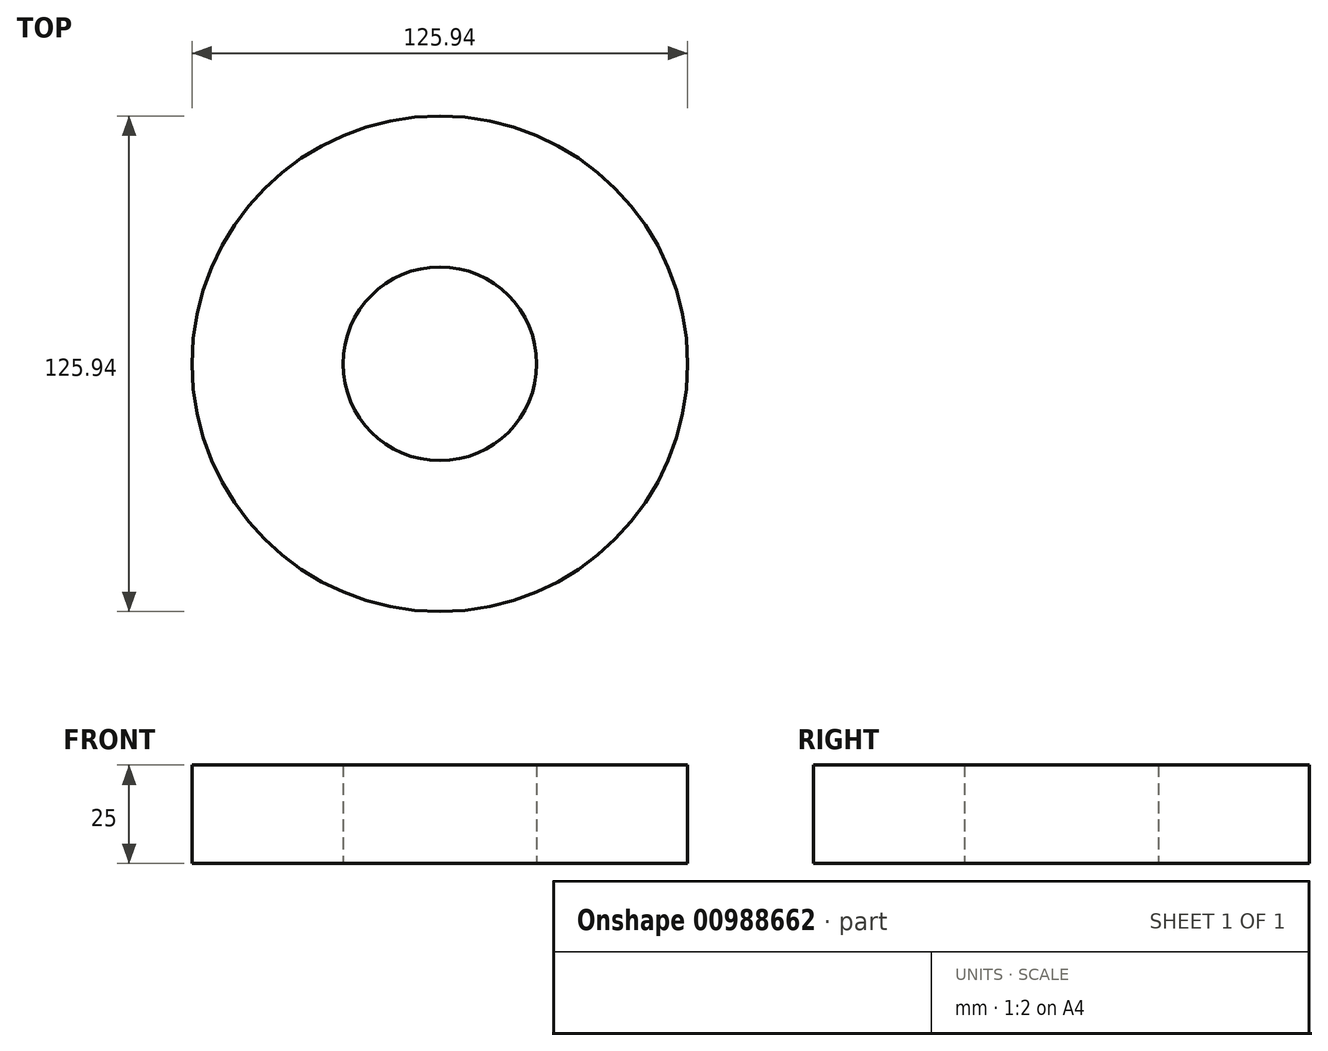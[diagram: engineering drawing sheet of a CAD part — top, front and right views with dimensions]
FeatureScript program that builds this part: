
annotation { "Feature Type Name" : "Feature", "Feature Type Description" : "" }
export const myFeature = defineFeature(function(context is Context, id is Id, definition is map)
    precondition{}
    {
        {
            var Q0;
            Q0=qCreatedBy(makeId("Top.planeOp"),FACE);
            var sketch = newSketch(context, id + "F0", { "sketchPlane" : qUnion([Q0])});
            skCircle(sketch, "E0", {"center": v(0, 0) * mm, "radius": 24.6 * mm});
            skSolve(sketch);
        }
        {
            var Q0;
            Q0=qCreatedBy(makeId("Top.planeOp"),FACE);
            var sketch = newSketch(context, id + "F1", { "sketchPlane" : qUnion([Q0])});
            skCircle(sketch, "E1", {"center": v(0, 0) * mm, "radius": 62.97 * mm});
            skSolve(sketch);
        }
        {
            var Q0;
            Q0 = qSketchRegion(id + "F0", true);
            var Q1;
            Q1 = qSketchRegion(id + "F1", true);
            extrude(context, id + "F2", {"entities" : qUnion([Q0, Q1]), "depth" : 25 * mm, "offsetDistance" : 25 * mm});
        }
    });
